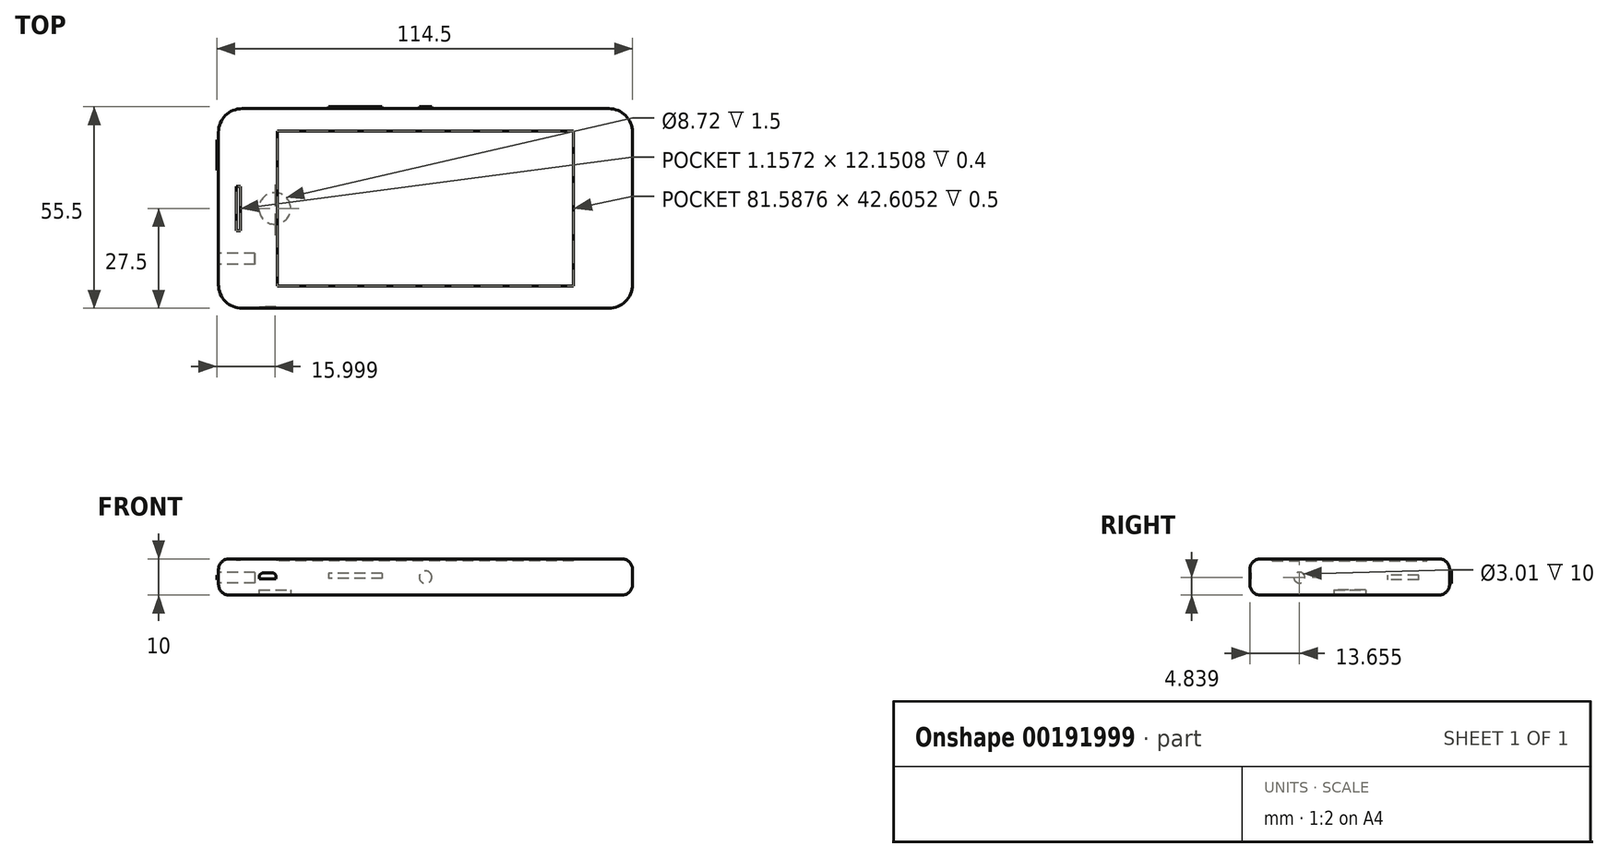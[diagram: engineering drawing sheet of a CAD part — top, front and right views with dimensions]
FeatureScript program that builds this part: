
annotation { "Feature Type Name" : "Feature", "Feature Type Description" : "" }
export const myFeature = defineFeature(function(context is Context, id is Id, definition is map)
    precondition{}
    {
        {
            var Q0;
            Q0=qCreatedBy(makeId("Top.planeOp"),FACE);
            var sketch = newSketch(context, id + "F0", { "sketchPlane" : qUnion([Q0])});
            skLineSegment(sketch, "E0.bottom", {"start": v(-57, 27.5) * mm, "end": v(57, 27.5) * mm});
            skLineSegment(sketch, "E0.top", {"start": v(-57, -27.5) * mm, "end": v(57, -27.5) * mm});
            skLineSegment(sketch, "E0.left", {"start": v(-57, 27.5) * mm, "end": v(-57, -27.5) * mm});
            skLineSegment(sketch, "E0.right", {"start": v(57, 27.5) * mm, "end": v(57, -27.5) * mm});
            skPoint(sketch, "E0.middle", {"position": v(0, 0) * mm});
            skSolve(sketch);
        }
        {
            var Q0;
            Q0=makeQuery(id+"F0.imprint","IMPRINT",FACE,{"disambiguationData":[TD([[makeQuery(id+"F0.imprint","IMPRINT",EDGE,{"derivedFrom":sQuery(id+"F0.wireOp",EDGE,"E0.bottom")}),-1.0]])]});
            extrude(context, id + "F1", {"entities" : qUnion([Q0]), "depth" : 10 * mm});
        }
        {
            var Q0;
            Q0=makeQuery(id+"F1.opExtrude","SWEPT_EDGE",EDGE,{"disambiguationData":[OSD([sQuery(id+"F0.wireOp",EDGE,"E0.top"),sQuery(id+"F0.wireOp",EDGE,"E0.right")])]});
            var Q1;
            Q1=makeQuery(id+"F1.opExtrude","SWEPT_EDGE",EDGE,{"disambiguationData":[OSD([sQuery(id+"F0.wireOp",EDGE,"E0.top"),sQuery(id+"F0.wireOp",EDGE,"E0.left")])]});
            var Q2;
            Q2=makeQuery(id+"F1.opExtrude","SWEPT_EDGE",EDGE,{"disambiguationData":[OSD([sQuery(id+"F0.wireOp",EDGE,"E0.bottom"),sQuery(id+"F0.wireOp",EDGE,"E0.right")])]});
            var Q3;
            Q3=makeQuery(id+"F1.opExtrude","SWEPT_EDGE",EDGE,{"disambiguationData":[OSD([sQuery(id+"F0.wireOp",EDGE,"E0.bottom"),sQuery(id+"F0.wireOp",EDGE,"E0.left")])]});
            fillet(context, id + "F2", {"entities" : qUnion([Q0, Q1, Q2, Q3]), "radius" : 6.52 * mm, "tangentPropagation" : true, "allowEdgeOverflow" : false});
        }
        {
            var Q0;
            {var subQ0=sQuery(id+"F0.wireOp",EDGE,"E0.right");var subQ1=sQuery(id+"F0.wireOp",EDGE,"E0.top");Q0=makeQuery(id+"F2.opFillet","BLEND_EDGE",EDGE,{"blendedFrom":[makeQuery(id+"F1.opExtrude","SWEPT_EDGE",EDGE,{"disambiguationData":[OSD([subQ1,subQ0])]}),makeQuery(id+"F1.opExtrude","CAP_FACE",FACE,{"disambiguationData":[OSD([sQuery(id+"F0.wireOp",EDGE,"E0.bottom"),subQ1,sQuery(id+"F0.wireOp",EDGE,"E0.left"),subQ0])],"isStart":true})],"blendedInto":[makeQuery(id+"F1.opExtrude","CAP_FACE",FACE,{"disambiguationData":[OSD([sQuery(id+"F0.wireOp",EDGE,"E0.bottom"),subQ1,sQuery(id+"F0.wireOp",EDGE,"E0.left"),subQ0])],"isStart":true})]});}
            var Q1;
            {var subQ0=sQuery(id+"F0.wireOp",EDGE,"E0.left");var subQ1=sQuery(id+"F0.wireOp",EDGE,"E0.top");Q1=makeQuery(id+"F2.opFillet","BLEND_EDGE",EDGE,{"blendedFrom":[makeQuery(id+"F1.opExtrude","SWEPT_EDGE",EDGE,{"disambiguationData":[OSD([subQ1,subQ0])]}),makeQuery(id+"F1.opExtrude","CAP_FACE",FACE,{"disambiguationData":[OSD([sQuery(id+"F0.wireOp",EDGE,"E0.bottom"),subQ1,subQ0,sQuery(id+"F0.wireOp",EDGE,"E0.right")])],"isStart":true})],"blendedInto":[makeQuery(id+"F1.opExtrude","CAP_FACE",FACE,{"disambiguationData":[OSD([sQuery(id+"F0.wireOp",EDGE,"E0.bottom"),subQ1,subQ0,sQuery(id+"F0.wireOp",EDGE,"E0.right")])],"isStart":true})]});}
            var Q2;
            {var subQ0=sQuery(id+"F0.wireOp",EDGE,"E0.left");var subQ1=sQuery(id+"F0.wireOp",EDGE,"E0.bottom");Q2=makeQuery(id+"F2.opFillet","BLEND_EDGE",EDGE,{"blendedFrom":[makeQuery(id+"F1.opExtrude","SWEPT_EDGE",EDGE,{"disambiguationData":[OSD([subQ1,subQ0])]}),makeQuery(id+"F1.opExtrude","CAP_FACE",FACE,{"disambiguationData":[OSD([subQ1,sQuery(id+"F0.wireOp",EDGE,"E0.top"),subQ0,sQuery(id+"F0.wireOp",EDGE,"E0.right")])],"isStart":true})],"blendedInto":[makeQuery(id+"F1.opExtrude","CAP_FACE",FACE,{"disambiguationData":[OSD([subQ1,sQuery(id+"F0.wireOp",EDGE,"E0.top"),subQ0,sQuery(id+"F0.wireOp",EDGE,"E0.right")])],"isStart":true})]});}
            var Q3;
            {var subQ0=sQuery(id+"F0.wireOp",EDGE,"E0.right");var subQ1=sQuery(id+"F0.wireOp",EDGE,"E0.bottom");Q3=makeQuery(id+"F2.opFillet","BLEND_EDGE",EDGE,{"blendedFrom":[makeQuery(id+"F1.opExtrude","SWEPT_EDGE",EDGE,{"disambiguationData":[OSD([subQ1,subQ0])]}),makeQuery(id+"F1.opExtrude","CAP_FACE",FACE,{"disambiguationData":[OSD([subQ1,sQuery(id+"F0.wireOp",EDGE,"E0.top"),sQuery(id+"F0.wireOp",EDGE,"E0.left"),subQ0])],"isStart":true})],"blendedInto":[makeQuery(id+"F1.opExtrude","CAP_FACE",FACE,{"disambiguationData":[OSD([subQ1,sQuery(id+"F0.wireOp",EDGE,"E0.top"),sQuery(id+"F0.wireOp",EDGE,"E0.left"),subQ0])],"isStart":true})]});}
            fillet(context, id + "F3", {"entities" : qUnion([Q0, Q1, Q2, Q3]), "radius" : 3 * mm, "tangentPropagation" : true, "allowEdgeOverflow" : false});
        }
        {
            var Q0;
            Q0=makeQuery(id+"F1.opExtrude","CAP_FACE",FACE,{"disambiguationData":[OSD([sQuery(id+"F0.wireOp",EDGE,"E0.bottom"),sQuery(id+"F0.wireOp",EDGE,"E0.top"),sQuery(id+"F0.wireOp",EDGE,"E0.left"),sQuery(id+"F0.wireOp",EDGE,"E0.right")])],"isStart":false});
            fillet(context, id + "F4", {"entities" : qUnion([Q0]), "radius" : 2.9 * mm, "tangentPropagation" : true, "allowEdgeOverflow" : false});
        }
        {
            var Q0;
            Q0=makeQuery(id+"F1.opExtrude","SWEPT_FACE",FACE,{"disambiguationData":[OSD([sQuery(id+"F0.wireOp",EDGE,"E0.bottom")])]});
            var sketch = newSketch(context, id + "F5", { "sketchPlane" : qUnion([Q0])});
            skCircle(sketch, "E1", {"center": v(0, 4.97) * mm, "radius": 1.73 * mm});
            skSolve(sketch);
        }
        {
            var Q0;
            Q0=makeQuery(id+"F5.imprint","IMPRINT",FACE,{"disambiguationData":[TD([[makeQuery(id+"F5.imprint","IMPRINT",EDGE,{"derivedFrom":sQuery(id+"F5.wireOp",EDGE,"E1")}),1.0]])]});
            extrude(context, id + "F6", {"entities" : qUnion([Q0]), "operationType" : NewBodyOperationType.ADD, "depth" : 0.5 * mm});
        }
        {
            var Q0;
            Q0=makeQuery(id+"F1.opExtrude","SWEPT_FACE",FACE,{"disambiguationData":[OSD([sQuery(id+"F0.wireOp",EDGE,"E0.bottom")])]});
            var sketch = newSketch(context, id + "F7", { "sketchPlane" : qUnion([Q0])});
            skLineSegment(sketch, "E2.bottom", {"start": v(11.94, 6.03) * mm, "end": v(26.73, 6.03) * mm});
            skLineSegment(sketch, "E2.top", {"start": v(11.94, 4.64) * mm, "end": v(26.73, 4.64) * mm});
            skLineSegment(sketch, "E2.left", {"start": v(11.94, 6.03) * mm, "end": v(11.94, 4.64) * mm});
            skLineSegment(sketch, "E2.right", {"start": v(26.73, 6.03) * mm, "end": v(26.73, 4.64) * mm});
            skPoint(sketch, "E2.middle", {"position": v(19.34, 5.34) * mm});
            skSolve(sketch);
        }
        {
            var Q0;
            Q0=makeQuery(id+"F7.imprint","IMPRINT",FACE,{"disambiguationData":[TD([[makeQuery(id+"F7.imprint","IMPRINT",EDGE,{"derivedFrom":sQuery(id+"F7.wireOp",EDGE,"E2.bottom")}),-1.0]])]});
            extrude(context, id + "F8", {"entities" : qUnion([Q0]), "operationType" : NewBodyOperationType.ADD, "depth" : 0.5 * mm});
        }
        {
            var Q0;
            Q0=makeQuery(id+"F1.opExtrude","CAP_FACE",FACE,{"disambiguationData":[OSD([sQuery(id+"F0.wireOp",EDGE,"E0.bottom"),sQuery(id+"F0.wireOp",EDGE,"E0.top"),sQuery(id+"F0.wireOp",EDGE,"E0.left"),sQuery(id+"F0.wireOp",EDGE,"E0.right")])],"isStart":true});
            var sketch = newSketch(context, id + "F9", { "sketchPlane" : qUnion([Q0])});
            skCircle(sketch, "E3", {"center": v(-41.5, 0) * mm, "radius": 4.36 * mm});
            skSolve(sketch);
        }
        {
            var Q0;
            Q0 = qSketchRegion(id + "F9", true);
            extrude(context, id + "F10", {"entities" : qUnion([Q0]), "operationType" : NewBodyOperationType.REMOVE, "oppositeDirection" : true, "depth" : 1.5 * mm});
        }
        {
            var Q0;
            Q0=makeQuery(id+"F1.opExtrude","CAP_FACE",FACE,{"disambiguationData":[OSD([sQuery(id+"F0.wireOp",EDGE,"E0.bottom"),sQuery(id+"F0.wireOp",EDGE,"E0.top"),sQuery(id+"F0.wireOp",EDGE,"E0.left"),sQuery(id+"F0.wireOp",EDGE,"E0.right")])],"isStart":false});
            var sketch = newSketch(context, id + "F11", { "sketchPlane" : qUnion([Q0])});
            skLineSegment(sketch, "E4.bottom", {"start": v(-50.95, 6.08) * mm, "end": v(-52.1, 6.08) * mm});
            skLineSegment(sketch, "E4.top", {"start": v(-50.95, -6.08) * mm, "end": v(-52.1, -6.08) * mm});
            skLineSegment(sketch, "E4.left", {"start": v(-50.95, 6.08) * mm, "end": v(-50.95, -6.08) * mm});
            skLineSegment(sketch, "E4.right", {"start": v(-52.1, 6.08) * mm, "end": v(-52.1, -6.08) * mm});
            skPoint(sketch, "E4.middle", {"position": v(-51.53, 0) * mm});
            skSolve(sketch);
        }
        {
            var Q0;
            Q0=makeQuery(id+"F11.imprint","IMPRINT",FACE,{"disambiguationData":[TD([[makeQuery(id+"F11.imprint","IMPRINT",EDGE,{"derivedFrom":sQuery(id+"F11.wireOp",EDGE,"E4.bottom")}),1.0]])]});
            extrude(context, id + "F12", {"entities" : qUnion([Q0]), "operationType" : NewBodyOperationType.REMOVE, "oppositeDirection" : true, "depth" : 0.4 * mm});
        }
        {
            var Q0;
            Q0=makeQuery(id+"F1.opExtrude","CAP_FACE",FACE,{"disambiguationData":[OSD([sQuery(id+"F0.wireOp",EDGE,"E0.bottom"),sQuery(id+"F0.wireOp",EDGE,"E0.top"),sQuery(id+"F0.wireOp",EDGE,"E0.left"),sQuery(id+"F0.wireOp",EDGE,"E0.right")])],"isStart":false});
            var sketch = newSketch(context, id + "F13", { "sketchPlane" : qUnion([Q0])});
            skLineSegment(sketch, "E5.bottom", {"start": v(40.8, -21.3) * mm, "end": v(-40.8, -21.3) * mm});
            skLineSegment(sketch, "E5.top", {"start": v(40.8, 21.3) * mm, "end": v(-40.8, 21.3) * mm});
            skLineSegment(sketch, "E5.left", {"start": v(40.8, -21.3) * mm, "end": v(40.8, 21.3) * mm});
            skLineSegment(sketch, "E5.right", {"start": v(-40.8, -21.3) * mm, "end": v(-40.8, 21.3) * mm});
            skPoint(sketch, "E5.middle", {"position": v(0, 0) * mm});
            skSolve(sketch);
        }
        {
            var Q0;
            Q0 = qSketchRegion(id + "F13", true);
            extrude(context, id + "F14", {"entities" : qUnion([Q0]), "operationType" : NewBodyOperationType.REMOVE, "oppositeDirection" : true, "depth" : 0.5 * mm});
        }
        {
            var Q0;
            Q0=makeQuery(id+"F1.opExtrude","SWEPT_FACE",FACE,{"disambiguationData":[OSD([sQuery(id+"F0.wireOp",EDGE,"E0.top")])]});
            var sketch = newSketch(context, id + "F15", { "sketchPlane" : qUnion([Q0])});
            skLineSegment(sketch, "E6", {"start": v(-44.97, 6.19) * mm, "end": v(-41.76, 6.19) * mm});
            skLineSegment(sketch, "E7", {"start": v(-41.76, 6.19) * mm, "end": v(-41.14, 5.55) * mm});
            skLineSegment(sketch, "E8", {"start": v(-41.14, 5.55) * mm, "end": v(-41.14, 4.46) * mm});
            skLineSegment(sketch, "E9", {"start": v(-41.14, 4.46) * mm, "end": v(-45.71, 4.46) * mm});
            skLineSegment(sketch, "E10", {"start": v(-45.71, 4.46) * mm, "end": v(-45.71, 5.55) * mm});
            skLineSegment(sketch, "E11", {"start": v(-45.71, 5.55) * mm, "end": v(-44.97, 6.19) * mm});
            skSolve(sketch);
        }
        {
            var Q0;
            Q0=makeQuery(id+"F15.imprint","IMPRINT",FACE,{"disambiguationData":[TD([[makeQuery(id+"F15.imprint","IMPRINT",EDGE,{"derivedFrom":sQuery(id+"F15.wireOp",EDGE,"E6")}),-1.0]])]});
            extrude(context, id + "F16", {"entities" : qUnion([Q0]), "operationType" : NewBodyOperationType.REMOVE, "oppositeDirection" : true, "depth" : 0.4 * mm});
        }
        {
            var Q0;
            Q0=makeQuery(id+"F1.opExtrude","SWEPT_FACE",FACE,{"disambiguationData":[OSD([sQuery(id+"F0.wireOp",EDGE,"E0.left")])]});
            var sketch = newSketch(context, id + "F17", { "sketchPlane" : qUnion([Q0])});
            skCircle(sketch, "E12", {"center": v(13.85, 4.84) * mm, "radius": 1.5 * mm});
            skSolve(sketch);
        }
        {
            var Q0;
            Q0=makeQuery(id+"F17.imprint","IMPRINT",FACE,{"disambiguationData":[TD([[makeQuery(id+"F17.imprint","IMPRINT",EDGE,{"derivedFrom":sQuery(id+"F17.wireOp",EDGE,"E12")}),1.0]])]});
            extrude(context, id + "F18", {"entities" : qUnion([Q0]), "operationType" : NewBodyOperationType.REMOVE, "oppositeDirection" : true, "depth" : 10 * mm});
        }
        {
            var Q0;
            Q0=makeQuery(id+"F1.opExtrude","SWEPT_FACE",FACE,{"disambiguationData":[OSD([sQuery(id+"F0.wireOp",EDGE,"E0.left")])]});
            var sketch = newSketch(context, id + "F19", { "sketchPlane" : qUnion([Q0])});
            skLineSegment(sketch, "E13.bottom", {"start": v(-18.97, 4.28) * mm, "end": v(-10.53, 4.28) * mm});
            skLineSegment(sketch, "E13.top", {"start": v(-18.97, 5.57) * mm, "end": v(-10.53, 5.57) * mm});
            skLineSegment(sketch, "E13.left", {"start": v(-18.97, 4.28) * mm, "end": v(-18.97, 5.57) * mm});
            skLineSegment(sketch, "E13.right", {"start": v(-10.53, 4.28) * mm, "end": v(-10.53, 5.57) * mm});
            skPoint(sketch, "E13.middle", {"position": v(-14.75, 4.93) * mm});
            skSolve(sketch);
        }
        {
            var Q0;
            Q0=makeQuery(id+"F19.imprint","IMPRINT",FACE,{"disambiguationData":[TD([[makeQuery(id+"F19.imprint","IMPRINT",EDGE,{"derivedFrom":sQuery(id+"F19.wireOp",EDGE,"E13.bottom")}),1.0]])]});
            extrude(context, id + "F20", {"entities" : qUnion([Q0]), "operationType" : NewBodyOperationType.ADD, "depth" : 0.5 * mm});
        }
    });
